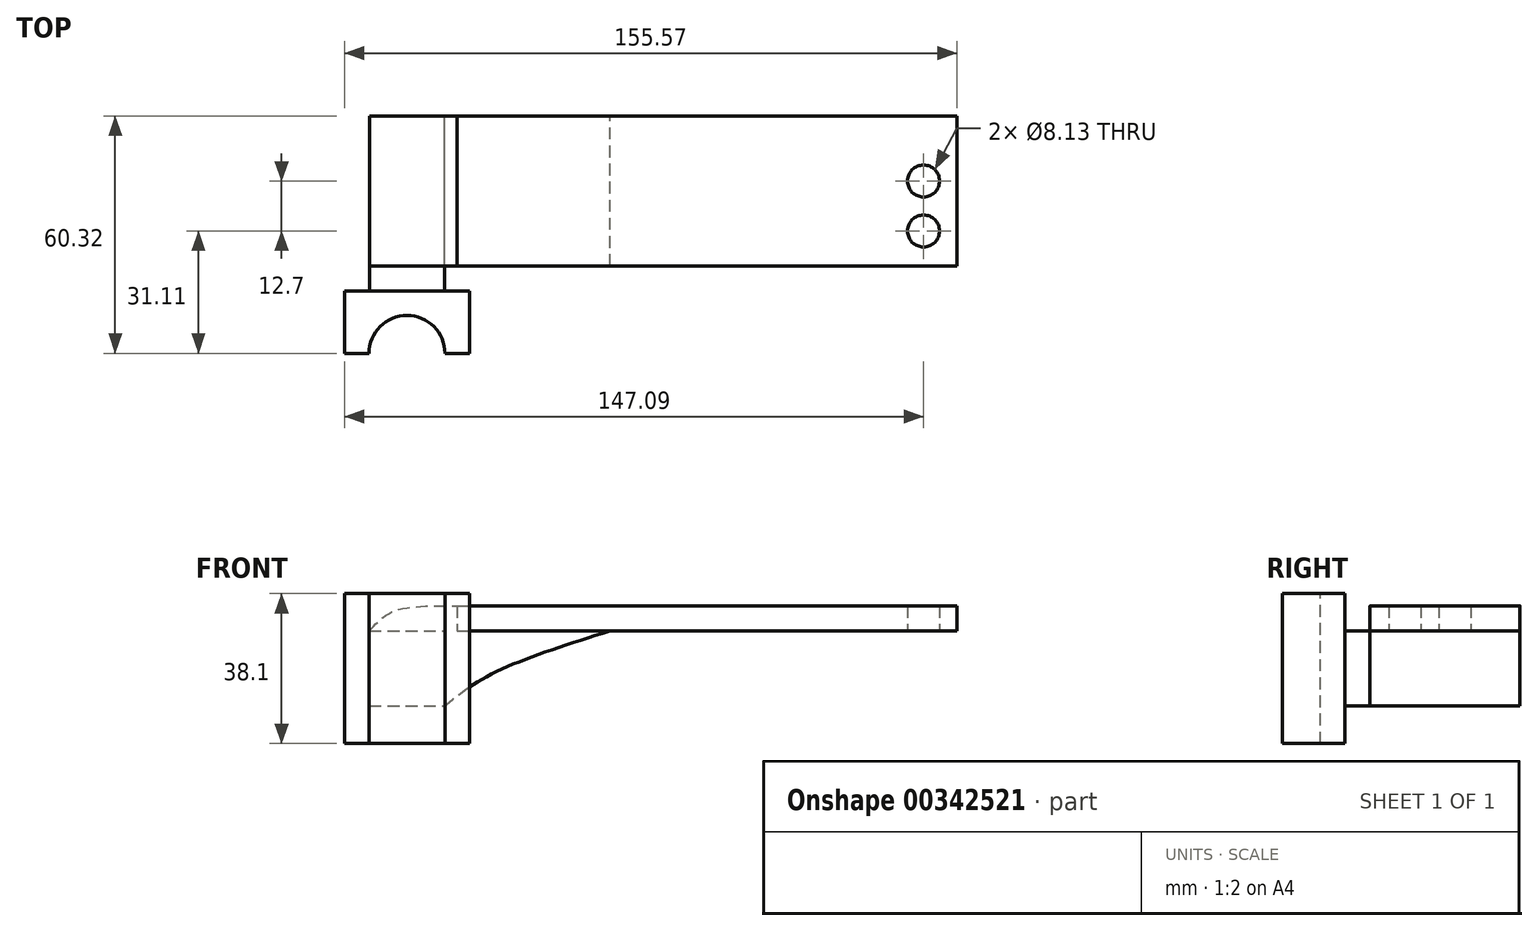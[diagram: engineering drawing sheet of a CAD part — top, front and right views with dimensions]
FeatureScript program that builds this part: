
annotation { "Feature Type Name" : "Feature", "Feature Type Description" : "" }
export const myFeature = defineFeature(function(context is Context, id is Id, definition is map)
    precondition{}
    {
        {
            var Q0;
            Q0=qCreatedBy(makeId("Front.planeOp"),FACE);
            var sketch = newSketch(context, id + "F0", { "sketchPlane" : qUnion([Q0])});
            skLineSegment(sketch, "E0.bottom", {"start": v(-75.77, -8.02) * mm, "end": v(-56.72, -8.02) * mm});
            skLineSegment(sketch, "E0.top", {"start": v(-75.77, -27.07) * mm, "end": v(-56.72, -27.07) * mm});
            skLineSegment(sketch, "E0.left", {"start": v(-75.77, -8.02) * mm, "end": v(-75.77, -27.07) * mm});
            skLineSegment(sketch, "E0.right", {"start": v(-56.72, -8.02) * mm, "end": v(-56.72, -27.07) * mm});
            skLineSegment(sketch, "E1.bottom", {"start": v(-53.55, -1.67) * mm, "end": v(73.45, -1.67) * mm});
            skLineSegment(sketch, "E1.top", {"start": v(-53.55, -8.02) * mm, "end": v(73.45, -8.02) * mm});
            skLineSegment(sketch, "E1.left", {"start": v(-53.55, -1.67) * mm, "end": v(-53.55, -8.02) * mm});
            skLineSegment(sketch, "E1.right", {"start": v(73.45, -1.67) * mm, "end": v(73.45, -8.02) * mm});
            skPoint(sketch, "E2", {"position": v(-66.25, -17.54) * mm});
            skPoint(sketch, "E2.positionSnap0", {"position": v(-66.25, -8.02) * mm});
            skPoint(sketch, "E3", {"position": v(-53.55, -4.84) * mm});
            skFitSpline(sketch, "E4", {"points": [v(-75.77, -8.02) * mm, v(-69.87, -3.08) * mm, v(-53.55, -1.67) * mm], "startDerivative": vector(11.88, 14.1) * mm, "endDerivative": vector(31.36, -0.5) * mm});
            skFitSpline(sketch, "E5", {"points": [v(-56.72, -27.07) * mm, v(-44.9, -19.02) * mm, v(-14.67, -8.02) * mm], "startDerivative": vector(25.39, 20.47) * mm, "endDerivative": vector(56.63, 17.8) * mm});
            skSolve(sketch);
        }
        {
            var Q0;
            {var subQ0=sQuery(id+"F0.wireOp",EDGE,"ce6e2a5a-d58e-4784-a380-edeeea4d48dd");var subQ1=sQuery(id+"F0.wireOp",EDGE,"E1.top");var subQ2=makeQuery(id+"F0.imprint","INTERSECT",VERTEX,{"disambiguationData":[OD(0.0)],"derivedFrom":[subQ1,subQ0]});Q0=makeQuery(id+"F0.imprint","IMPRINT",FACE,{"disambiguationData":[TD([[makeQuery(id+"F0.imprint","IMPRINT",EDGE,{"disambiguationData":[TD([[subQ2,1.0]])],"derivedFrom":subQ1}),1.0]])]});}
            extrude(context, id + "F1", {"entities" : qUnion([Q0]), "endBound" : BoundingType.SYMMETRIC, "depth" : 38.1 * mm});
        }
        {
            var Q0;
            Q0=makeQuery(id+"F0.imprint","IMPRINT",FACE,{"disambiguationData":[TD([[makeQuery(id+"F0.imprint","IMPRINT",EDGE,{"derivedFrom":sQuery(id+"F0.wireOp",EDGE,"E0.bottom")}),1.0]])]});
            extrude(context, id + "F2", {"entities" : qUnion([Q0]), "endBound" : BoundingType.SYMMETRIC, "depth" : 38.1 * mm});
        }
        {
            var Q0;
            Q0=makeQuery(id+"F0.imprint","IMPRINT",FACE,{"disambiguationData":[TD([[makeQuery(id+"F0.imprint","IMPRINT",EDGE,{"derivedFrom":sQuery(id+"F0.wireOp",EDGE,"E0.bottom")}),-1.0]])]});
            extrude(context, id + "F3", {"entities" : qUnion([Q0]), "depth" : 25.4 * mm, "hasSecondDirection" : true, "secondDirectionOppositeDirection" : true, "secondDirectionDepth" : 19.05 * mm});
        }
        {
            var Q0;
            Q0=makeQuery(id+"F3.opExtrude","CAP_FACE",FACE,{"disambiguationData":[OSD([sQuery(id+"F0.wireOp",EDGE,"E0.bottom"),sQuery(id+"F0.wireOp",EDGE,"E0.top"),sQuery(id+"F0.wireOp",EDGE,"E0.left"),sQuery(id+"F0.wireOp",EDGE,"E0.right")])],"isStart":false});
            var sketch = newSketch(context, id + "F4", { "sketchPlane" : qUnion([Q0])});
            skLineSegment(sketch, "E6.bottom", {"start": v(-82.12, 1.5) * mm, "end": v(-50.37, 1.5) * mm});
            skLineSegment(sketch, "E6.top", {"start": v(-82.12, -36.6) * mm, "end": v(-50.37, -36.6) * mm});
            skLineSegment(sketch, "E6.left", {"start": v(-82.12, 1.5) * mm, "end": v(-82.12, -36.6) * mm});
            skLineSegment(sketch, "E6.right", {"start": v(-50.37, 1.5) * mm, "end": v(-50.37, -36.6) * mm});
            skPoint(sketch, "E6.middle", {"position": v(-66.25, -17.54) * mm});
            skSolve(sketch);
        }
        {
            var Q0;
            Q0=makeQuery(id+"F4.imprint","IMPRINT",FACE,{"disambiguationData":[TD([[makeQuery(id+"F4.imprint","IMPRINT",EDGE,{"derivedFrom":sQuery(id+"F4.wireOp",EDGE,"E6.bottom")}),-1.0]])]});
            var Q1;
            {var subQ3=sQuery(id+"F0.wireOp",EDGE,"E0.bottom");Q1=makeQuery(id+"F4.imprint","IMPRINT",FACE,{"disambiguationData":[TD([[makeQuery(id+"F4.imprint","IMPRINT",EDGE,{"derivedFrom":makeQuery(id+"F3.opExtrude","CAP_EDGE",EDGE,{"disambiguationData":[OSD([subQ3])],"isStart":false})}),-1.0]])]});}
            extrude(context, id + "F5", {"entities" : qUnion([Q0, Q1]), "depth" : 15.88 * mm});
        }
        {
            var Q0;
            Q0=makeQuery(id+"F5.opExtrude","SWEPT_FACE",FACE,{"disambiguationData":[OSD([sQuery(id+"F4.wireOp",EDGE,"E6.bottom")])]});
            var sketch = newSketch(context, id + "F6", { "sketchPlane" : qUnion([Q0])});
            skPoint(sketch, "E7", {"position": v(-66.25, -41.28) * mm});
            skSolve(sketch);
        }
        {
            var Q0;
            Q0=sQuery(id+"F6.wireOp",VERTEX,"E7");
            var Q1;
            Q1=makeQuery(id+"F5.opExtrude","SWEPT_BODY",BODY,{"disambiguationData":[OSD([sQuery(id+"F4.wireOp",EDGE,"E6.bottom"),sQuery(id+"F4.wireOp",EDGE,"E6.top"),sQuery(id+"F4.wireOp",EDGE,"E6.left"),sQuery(id+"F4.wireOp",EDGE,"E6.right")])]});
            hole(context, id + "F7", {"style" : HoleStyle.SIMPLE, "endStyle" : HoleEndStyle.THROUGH, "holeDiameter" : 19.3 * mm, "isTappedThrough" : true, "tappedDepth" : 12.7 * mm, "tapClearance" : 3, "locations" : qUnion([Q0]), "scope" : qUnion([Q1])});
        }
        {
            var Q0;
            Q0=makeQuery(id+"F1.opExtrude","SWEPT_FACE",FACE,{"disambiguationData":[OSD([sQuery(id+"F0.wireOp",EDGE,"E1.top")])]});
            var sketch = newSketch(context, id + "F8", { "sketchPlane" : qUnion([Q0])});
            skPoint(sketch, "E8", {"position": v(64.97, -2.54) * mm});
            skPoint(sketch, "E9", {"position": v(64.97, 10.16) * mm});
            skSolve(sketch);
        }
        {
            var Q0;
            Q0=sQuery(id+"F8.wireOp",VERTEX,"E9");
            var Q1;
            Q1=sQuery(id+"F8.wireOp",VERTEX,"E8");
            var Q2;
            Q2=makeQuery(id+"F1.opExtrude","SWEPT_BODY",BODY,{"disambiguationData":[OSD([sQuery(id+"F0.wireOp",EDGE,"E1.bottom"),sQuery(id+"F0.wireOp",EDGE,"E1.top"),sQuery(id+"F0.wireOp",EDGE,"E1.left"),sQuery(id+"F0.wireOp",EDGE,"E1.right")])]});
            hole(context, id + "F9", {"style" : HoleStyle.SIMPLE, "endStyle" : HoleEndStyle.THROUGH, "holeDiameter" : 8.13 * mm, "isTappedThrough" : true, "tappedDepth" : 12.7 * mm, "tapClearance" : 3, "locations" : qUnion([Q0, Q1]), "scope" : qUnion([Q2])});
        }
    });
